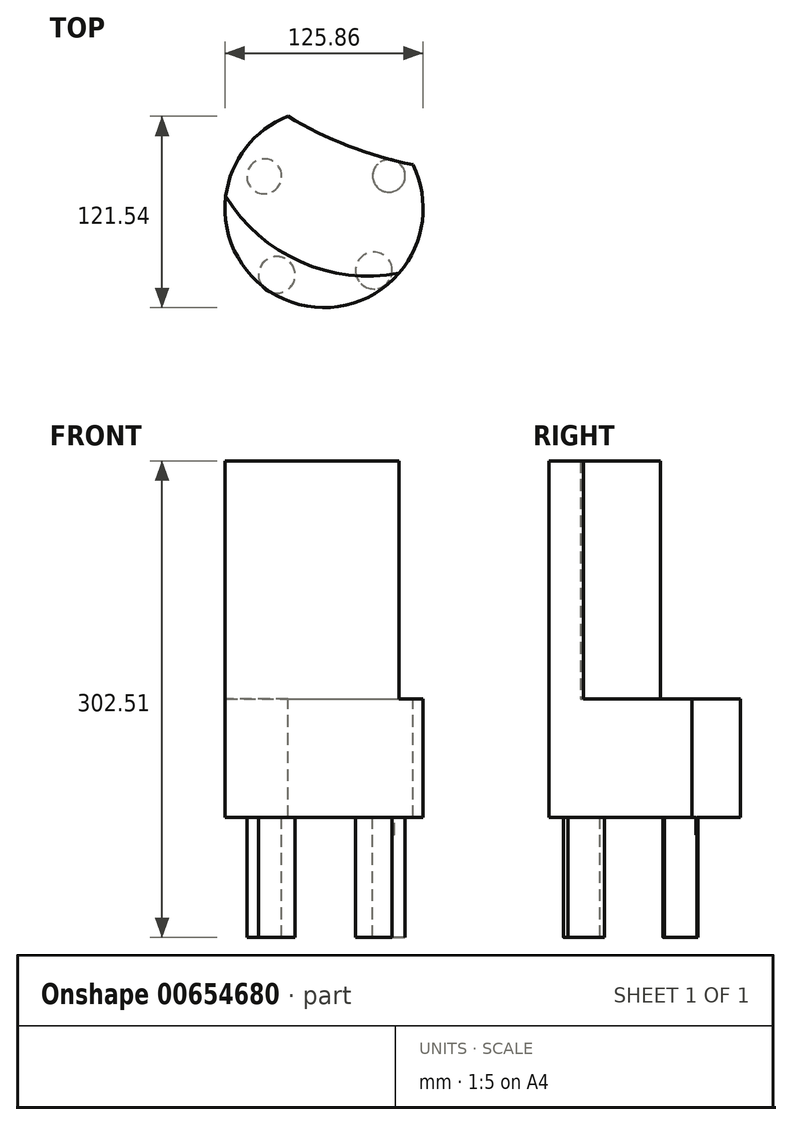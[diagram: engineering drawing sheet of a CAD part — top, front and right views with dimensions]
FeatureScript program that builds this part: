
annotation { "Feature Type Name" : "Feature", "Feature Type Description" : "" }
export const myFeature = defineFeature(function(context is Context, id is Id, definition is map)
    precondition{}
    {
        {
            var Q0;
            Q0=qCreatedBy(makeId("Top.planeOp"),FACE);
            var sketch = newSketch(context, id + "F0", { "sketchPlane" : qUnion([Q0])});
            skCircle(sketch, "E0", {"center": v(0, 0) * mm, "radius": 62.93 * mm});
            skSolve(sketch);
        }
        {
            var Q0;
            Q0 = qSketchRegion(id + "F0", true);
            extrude(context, id + "F1", {"entities" : qUnion([Q0]), "depth" : 75.18 * mm, "offsetDistance" : 25.4 * mm});
        }
        {
            var Q0;
            Q0=makeQuery(id+"F1.opExtrude","CAP_FACE",FACE,{"disambiguationData":[OSD([sQuery(id+"F0.wireOp",EDGE,"E0")])],"isStart":false});
            var sketch = newSketch(context, id + "F2", { "sketchPlane" : qUnion([Q0])});
            skArc(sketch, "E1", {"start": v(-62.45, 7.78) * mm, "mid": v(-14.99, -33.84) * mm, "end": v(47.73, -41.02) * mm});
            skSolve(sketch);
        }
        {
            var Q0;
            Q0 = qSketchRegion(id + "F2", true);
            var Q1;
            {var subQ0=sQuery(id+"F2.wireOp",EDGE,"E1");Q1=makeQuery(id+"F2.imprint","IMPRINT",FACE,{"disambiguationData":[TD([[makeQuery(id+"F2.imprint","IMPRINT",EDGE,{"derivedFrom":subQ0}),-1.0]])]});}
            extrude(context, id + "F3", {"entities" : qUnion([Q0, Q1]), "operationType" : NewBodyOperationType.ADD, "depth" : 151.13 * mm, "offsetDistance" : 25.4 * mm});
        }
        {
            var Q0;
            Q0=makeQuery(id+"F1.opExtrude","CAP_FACE",FACE,{"disambiguationData":[OSD([sQuery(id+"F0.wireOp",EDGE,"E0")])],"isStart":true});
            var sketch = newSketch(context, id + "F4", { "sketchPlane" : qUnion([Q0])});
            skCircle(sketch, "E2", {"center": v(41.2, -20.7) * mm, "radius": 10.35 * mm});
            skCircle(sketch, "E3", {"center": v(-37.95, -20.4) * mm, "radius": 11.09 * mm});
            skCircle(sketch, "E4", {"center": v(-30, 42.21) * mm, "radius": 11.66 * mm});
            skCircle(sketch, "E5", {"center": v(31.64, 39.43) * mm, "radius": 11.66 * mm});
            skSolve(sketch);
        }
        {
            var Q0;
            Q0=makeQuery(id+"F4.imprint","IMPRINT",FACE,{"disambiguationData":[TD([[makeQuery(id+"F4.imprint","IMPRINT",EDGE,{"derivedFrom":sQuery(id+"F4.wireOp",EDGE,"E2")}),1.0]])]});
            var Q1;
            Q1=makeQuery(id+"F4.imprint","IMPRINT",FACE,{"disambiguationData":[TD([[makeQuery(id+"F4.imprint","IMPRINT",EDGE,{"derivedFrom":sQuery(id+"F4.wireOp",EDGE,"E3")}),1.0]])]});
            var Q2;
            {var subQ0=sQuery(id+"F4.wireOp",EDGE,"E4");var subQ1=makeQuery(id+"F1.opExtrude","CAP_EDGE",EDGE,{"disambiguationData":[OSD([sQuery(id+"F0.wireOp",EDGE,"E0")])],"isStart":true});var subQ2=makeQuery(id+"F4.imprint","INTERSECT",VERTEX,{"disambiguationData":[OD(0.0)],"derivedFrom":[subQ1,subQ0]});Q2=makeQuery(id+"F4.imprint","IMPRINT",FACE,{"disambiguationData":[TD([[makeQuery(id+"F4.imprint","IMPRINT",EDGE,{"disambiguationData":[TD([[subQ2,1.0]])],"derivedFrom":subQ0}),1.0]])]});}
            var Q3;
            {var subQ0=sQuery(id+"F4.wireOp",EDGE,"E4");var subQ1=makeQuery(id+"F1.opExtrude","CAP_EDGE",EDGE,{"disambiguationData":[OSD([sQuery(id+"F0.wireOp",EDGE,"E0")])],"isStart":true});var subQ2=makeQuery(id+"F4.imprint","INTERSECT",VERTEX,{"disambiguationData":[OD(0.0)],"derivedFrom":[subQ1,subQ0]});Q3=makeQuery(id+"F4.imprint","IMPRINT",FACE,{"disambiguationData":[TD([[makeQuery(id+"F4.imprint","IMPRINT",EDGE,{"disambiguationData":[TD([[subQ2,-1.0]])],"derivedFrom":subQ0}),1.0]])]});}
            var Q4;
            Q4=makeQuery(id+"F4.imprint","IMPRINT",FACE,{"disambiguationData":[TD([[makeQuery(id+"F4.imprint","IMPRINT",EDGE,{"derivedFrom":sQuery(id+"F4.wireOp",EDGE,"E5")}),1.0]])]});
            extrude(context, id + "F5", {"entities" : qUnion([Q0, Q1, Q2, Q3, Q4]), "operationType" : NewBodyOperationType.ADD, "depth" : 76.2 * mm, "offsetDistance" : 25.4 * mm});
        }
        {
            var Q0;
            Q0=makeQuery(id+"F1.opExtrude","CAP_FACE",FACE,{"disambiguationData":[OSD([sQuery(id+"F0.wireOp",EDGE,"E0")])],"isStart":false});
            var sketch = newSketch(context, id + "F6", { "sketchPlane" : qUnion([Q0])});
            skArc(sketch, "E6", {"start": v(-22.92, 58.6) * mm, "mid": v(15.43, 39.75) * mm, "end": v(56.46, 27.8) * mm});
            skSolve(sketch);
        }
        {
            var Q0;
            {var subQ0=sQuery(id+"F6.wireOp",EDGE,"E6");Q0=makeQuery(id+"F6.imprint","IMPRINT",FACE,{"disambiguationData":[TD([[makeQuery(id+"F6.imprint","IMPRINT",EDGE,{"derivedFrom":subQ0}),1.0]])]});}
            extrude(context, id + "F7", {"entities" : qUnion([Q0]), "operationType" : NewBodyOperationType.REMOVE, "oppositeDirection" : true, "depth" : 86.36 * mm, "offsetDistance" : 25.4 * mm});
        }
    });
